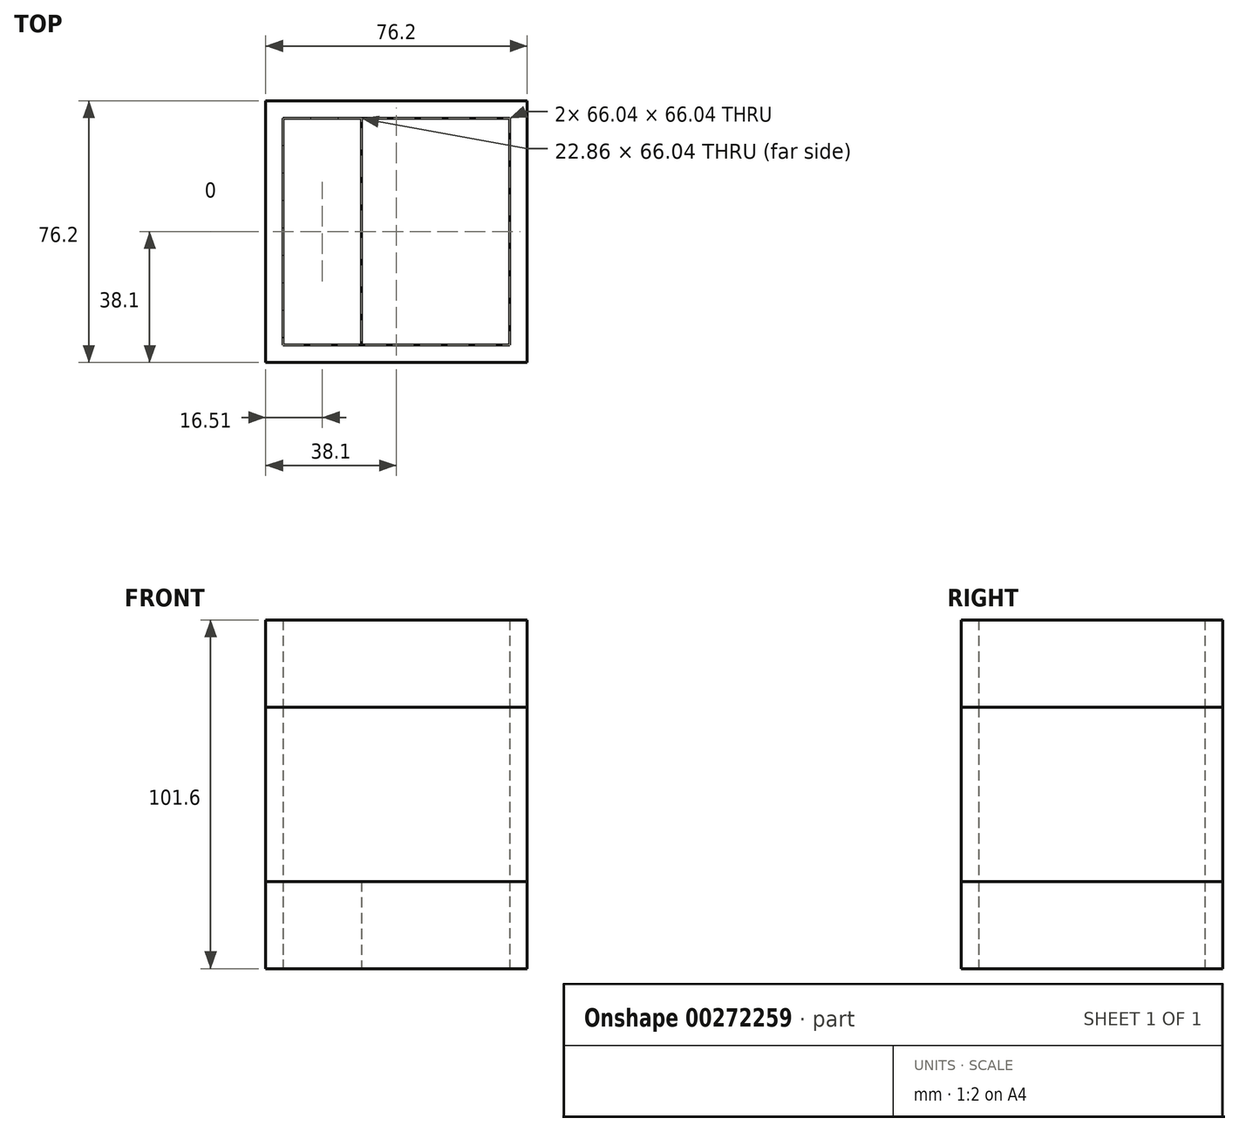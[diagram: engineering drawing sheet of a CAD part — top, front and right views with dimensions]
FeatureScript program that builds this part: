
annotation { "Feature Type Name" : "Feature", "Feature Type Description" : "" }
export const myFeature = defineFeature(function(context is Context, id is Id, definition is map)
    precondition{}
    {
        {
            var Q0;
            Q0=qCreatedBy(makeId("Top.planeOp"),FACE);
            var sketch = newSketch(context, id + "F0", { "sketchPlane" : qUnion([Q0])});
            skLineSegment(sketch, "E0.bottom", {"start": v(38.1, 38.1) * mm, "end": v(-38.1, 38.1) * mm});
            skLineSegment(sketch, "E0.top", {"start": v(38.1, -38.1) * mm, "end": v(-38.1, -38.1) * mm});
            skLineSegment(sketch, "E0.left", {"start": v(38.1, 38.1) * mm, "end": v(38.1, -38.1) * mm});
            skLineSegment(sketch, "E0.right", {"start": v(-38.1, 38.1) * mm, "end": v(-38.1, -38.1) * mm});
            skPoint(sketch, "E0.middle", {"position": v(0, 0) * mm});
            skLineSegment(sketch, "E1.bottom", {"start": v(33.02, 33.02) * mm, "end": v(-33.02, 33.02) * mm});
            skLineSegment(sketch, "E1.top", {"start": v(33.02, -33.02) * mm, "end": v(-33.02, -33.02) * mm});
            skLineSegment(sketch, "E1.left", {"start": v(33.02, 33.02) * mm, "end": v(33.02, -33.02) * mm});
            skLineSegment(sketch, "E1.right", {"start": v(-33.02, 33.02) * mm, "end": v(-33.02, -33.02) * mm});
            skLineSegment(sketch, "E2.bottom", {"start": v(-15.24, 33.02) * mm, "end": v(-10.16, 33.02) * mm});
            skLineSegment(sketch, "E2.top", {"start": v(-15.24, -33.02) * mm, "end": v(-10.16, -33.02) * mm});
            skLineSegment(sketch, "E2.left", {"start": v(-15.24, 33.02) * mm, "end": v(-15.24, -33.02) * mm});
            skLineSegment(sketch, "E2.right", {"start": v(-10.16, 33.02) * mm, "end": v(-10.16, -33.02) * mm});
            skSolve(sketch);
        }
        {
            var Q0;
            Q0=makeQuery(id+"F0.imprint","IMPRINT",FACE,{"disambiguationData":[TD([[makeQuery(id+"F0.imprint","IMPRINT",EDGE,{"derivedFrom":sQuery(id+"F0.wireOp",EDGE,"E0.bottom")}),1.0]])]});
            var Q1;
            Q1=makeQuery(id+"F0.imprint","IMPRINT",FACE,{"disambiguationData":[TD([[makeQuery(id+"F0.imprint","IMPRINT",EDGE,{"derivedFrom":sQuery(id+"F0.wireOp",EDGE,"E2.bottom")}),-1.0]])]});
            extrude(context, id + "F1", {"entities" : qUnion([Q0, Q1]), "depth" : 76.2 * mm});
        }
        {
            var Q0;
            Q0 = qSketchRegion(id + "F0", true);
            var Q1;
            Q1 = qSketchRegion(id + "FFrqAV9Y8b7q3u7_1", true);
            var Q2;
            Q2=makeQuery(id+"F1.opExtrude","CAP_FACE",FACE,{"disambiguationData":[OSD([sQuery(id+"F0.wireOp",EDGE,"E0.bottom"),sQuery(id+"F0.wireOp",EDGE,"E0.top"),sQuery(id+"F0.wireOp",EDGE,"E0.left"),sQuery(id+"F0.wireOp",EDGE,"E0.right"),sQuery(id+"F0.wireOp",EDGE,"E1.bottom"),sQuery(id+"F0.wireOp",EDGE,"E1.top"),sQuery(id+"F0.wireOp",EDGE,"E1.left"),sQuery(id+"F0.wireOp",EDGE,"E1.right"),sQuery(id+"F0.wireOp",EDGE,"E2.left"),sQuery(id+"F0.wireOp",EDGE,"E2.right")])],"isStart":false});
            var Q3;
            {var subQ0=sQuery(id+"F0.wireOp",EDGE,"E1.left");Q3=makeQuery(id+"F0.imprint","IMPRINT",FACE,{"disambiguationData":[TD([[makeQuery(id+"F0.imprint","IMPRINT",EDGE,{"derivedFrom":subQ0}),-1.0]])]});}
            extrude(context, id + "F2", {"entities" : qUnion([Q0, Q1, Q2, Q3]), "depth" : 25.4 * mm});
        }
    });
